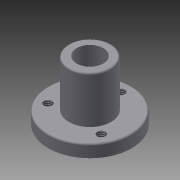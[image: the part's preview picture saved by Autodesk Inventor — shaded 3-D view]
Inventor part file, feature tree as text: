
AUTODESK INVENTOR PART (.ipt)
format: ipt  version: 2015 (Build 190159000, 159)  size: 116,224 bytes
history: native  units: mm
features: sketch x4, extrude x2, hole x2, fillet x1
ambient origin geometry x8: Origin, YZ Plane, XZ Plane, XY Plane, X Axis, Y Axis, Z Axis, Center Point
bodies: Solid1 (feature_tree)
feature tree (9):
  extrude  "Extrusion1"  Depth=3.75mm TaperAngle=0.0deg
  extrude  "Extrusion2"  Depth=14.0mm TaperAngle=0.0deg
  hole  "Hole1"  [1 undecoded]
  hole  "Hole2"  [1 undecoded]
  fillet  "Fillet1"  [1 undecoded]
  sketch  "Sketch1"  dims[d0=25.0mm d1=3.75mm d2=0.0mm]
  sketch  "Sketch2"  dims[d3=12.7mm d4=14.0mm d5=0.0mm]
  sketch  "Sketch3"  dims[d6=8.0mm d7=6.0mm d8=4.0mm d9=2.0mm d10=90.0deg d11=8.0mm d12=20.594885mm d13=16.0mm]
  sketch  "Sketch4"  dims[d14=2.459mm d15=6.0mm d16=4.0mm d17=2.0mm d18=90.0deg d19=8.0mm d20=20.594885mm d21=0.5mm]
note: 3 required parameter values undecoded (feature->parameter linkage not recoverable at this tier; creation-order binding heuristic only, values carry confidence <= 0.55)
